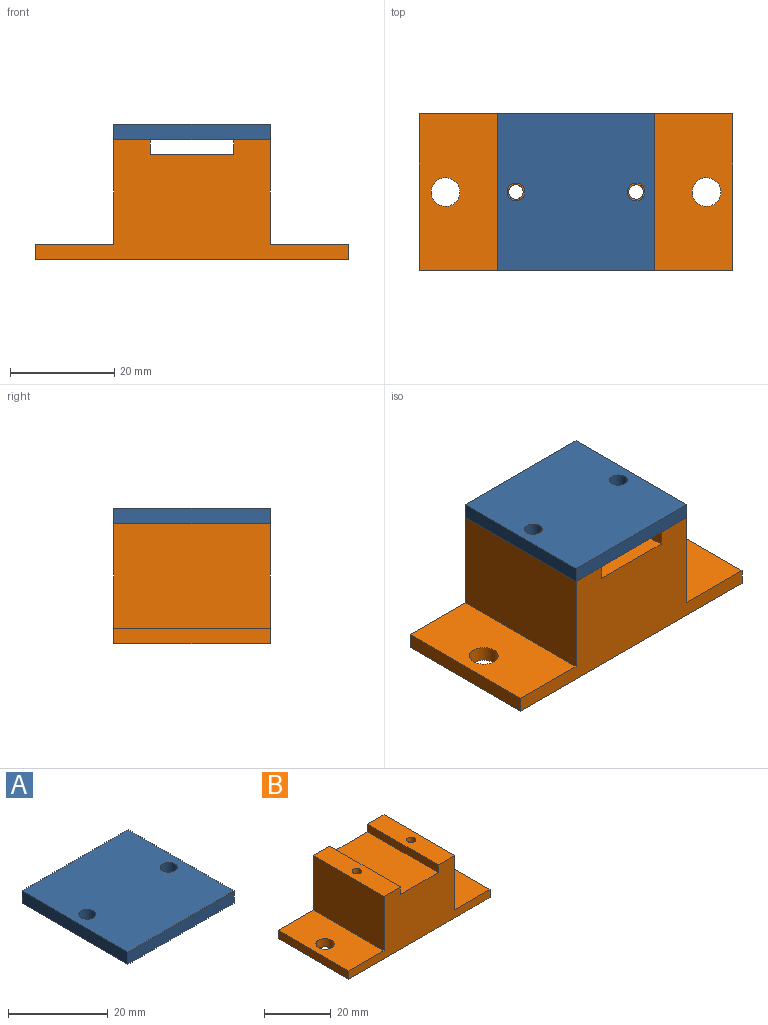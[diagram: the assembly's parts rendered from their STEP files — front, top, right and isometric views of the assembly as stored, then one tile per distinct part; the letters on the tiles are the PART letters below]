
ASSEMBLY  parts=2 mates=1
PART A: 8 faces, bbox 30x30x3 mm
  f0: plane 30x3mm, normal (0,-1,0), area 90mm2, adj f1,f5,f6,f7
  f1: plane 30x3mm, normal (1,0,0), area 90mm2, adj f0,f2,f6,f7
  f2: plane 30x3mm, normal (0,1,0), area 90mm2, adj f1,f5,f6,f7
  f3: cylinder r=1.7mm len=3.4mm, axis (0,0,-1), area 32mm2, adj f6,f7
  f4: cylinder r=1.7mm len=3.4mm, axis (0,0,-1), area 32mm2, adj f6,f7
  f5: plane 30x3mm, normal (-1,0,0), area 90mm2, adj f0,f2,f6,f7
  f6: plane 30x30mm, normal (0,0,1), area 881.8mm2, adj f0,f1,f2,f3,f4,f5
  f7: plane 30x30mm, normal (0,0,-1), area 881.8mm2, adj f0,f1,f2,f3,f4,f5
PART B: 18 faces, bbox 60x30x23 mm
  f0: plane 30x6.95mm, normal (0,0,1), area 202.3mm2, adj f1,f4,f11,f14,f17
  f1: plane 60x23mm, normal (0,-1,0), area 734.9mm2, adj f0,f2,f3,f7,f8,f9,f10,f11
  f2: plane 30x15mm, normal (0,0,1), area 426.2mm2, adj f1,f4,f5,f7,f11
  f3: plane 30x3mm, normal (1,0,0), area 90mm2, adj f1,f4,f8,f9
  f4: plane 60x23mm, normal (0,1,0), area 734.9mm2, adj f0,f2,f3,f7,f8,f9,f10,f11
  f5: cylinder r=2.75mm len=5.5mm, axis (0,0,-1), area 51.8mm2, adj f2,f9
  f6: cylinder r=2.75mm len=5.5mm, axis (0,0,-1), area 51.8mm2, adj f8,f9
  f7: plane 30x3mm, normal (-1,0,0), area 90mm2, adj f1,f2,f4,f9
  f8: plane 30x15mm, normal (0,0,1), area 426.2mm2, adj f1,f3,f4,f6,f10
  f9: plane 60x30mm, normal (0,0,-1), area 1740.2mm2, adj f1,f3,f4,f5,f6,f7,f16,f17
  f10: plane 30x20mm, normal (1,0,0), area 600mm2, adj f1,f4,f8,f12
  f11: plane 30x20mm, normal (-1,0,0), area 600mm2, adj f0,f1,f2,f4
  f12: plane 30x6.95mm, normal (0,0,1), area 202.3mm2, adj f1,f4,f10,f13,f16
  f13: plane 30x2.8mm, normal (-1,0,0), area 84mm2, adj f1,f4,f12,f15
  f14: plane 30x2.8mm, normal (1,0,0), area 84mm2, adj f0,f1,f4,f15
  f15: plane 30x16.1mm, normal (0,0,1), area 483mm2, adj f1,f4,f13,f14
  f16: cylinder r=1.4mm len=23mm, axis (0,0,1), area 202.3mm2, adj f9,f12
  f17: cylinder r=1.4mm len=23mm, axis (0,0,1), area 202.3mm2, adj f0,f9
PLACE A rot(axis=(1,0,0),180deg) t=(-5.44,3.6,24.61)mm
PLACE B t=(-5.44,3.6,-1.39)mm
MATE fastened A.f4 <-> B.f16  axis (0,0,-1) through (6.08,3.6,21.61)mm
